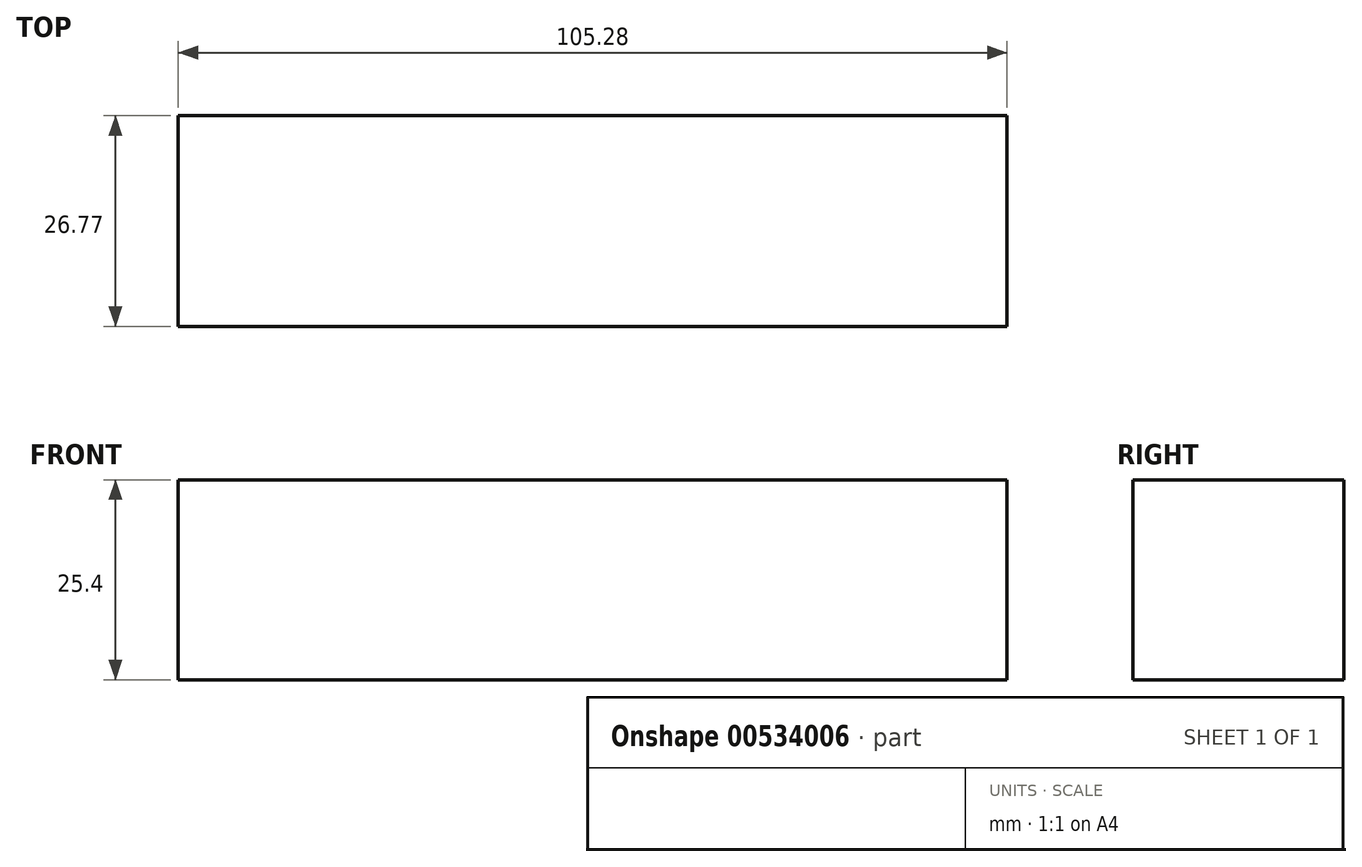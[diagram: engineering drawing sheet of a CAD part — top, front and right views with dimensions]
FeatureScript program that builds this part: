
annotation { "Feature Type Name" : "Feature", "Feature Type Description" : "" }
export const myFeature = defineFeature(function(context is Context, id is Id, definition is map)
    precondition{}
    {
        {
            var Q0;
            Q0=qCreatedBy(makeId("Top.planeOp"),FACE);
            var sketch = newSketch(context, id + "F0", { "sketchPlane" : qUnion([Q0])});
            skLineSegment(sketch, "E0", {"start": v(-41.2, 0) * mm, "end": v(-41.2, 26.77) * mm});
            skLineSegment(sketch, "E1", {"start": v(-41.2, 26.77) * mm, "end": v(64.07, 26.77) * mm});
            skLineSegment(sketch, "E2", {"start": v(64.07, 26.77) * mm, "end": v(64.07, 0) * mm});
            skLineSegment(sketch, "E3", {"start": v(64.07, 0) * mm, "end": v(-41.2, 0) * mm});
            skSolve(sketch);
        }
        {
            var Q0;
            Q0=makeQuery(id+"F0.imprint","IMPRINT",FACE,{"disambiguationData":[TD([[makeQuery(id+"F0.imprint","IMPRINT",EDGE,{"derivedFrom":sQuery(id+"F0.wireOp",EDGE,"E0")}),-1.0]])]});
            extrude(context, id + "F1", {"entities" : qUnion([Q0]), "oppositeDirection" : true, "depth" : 25.4 * mm, "offsetDistance" : 25.4 * mm});
        }
    });
